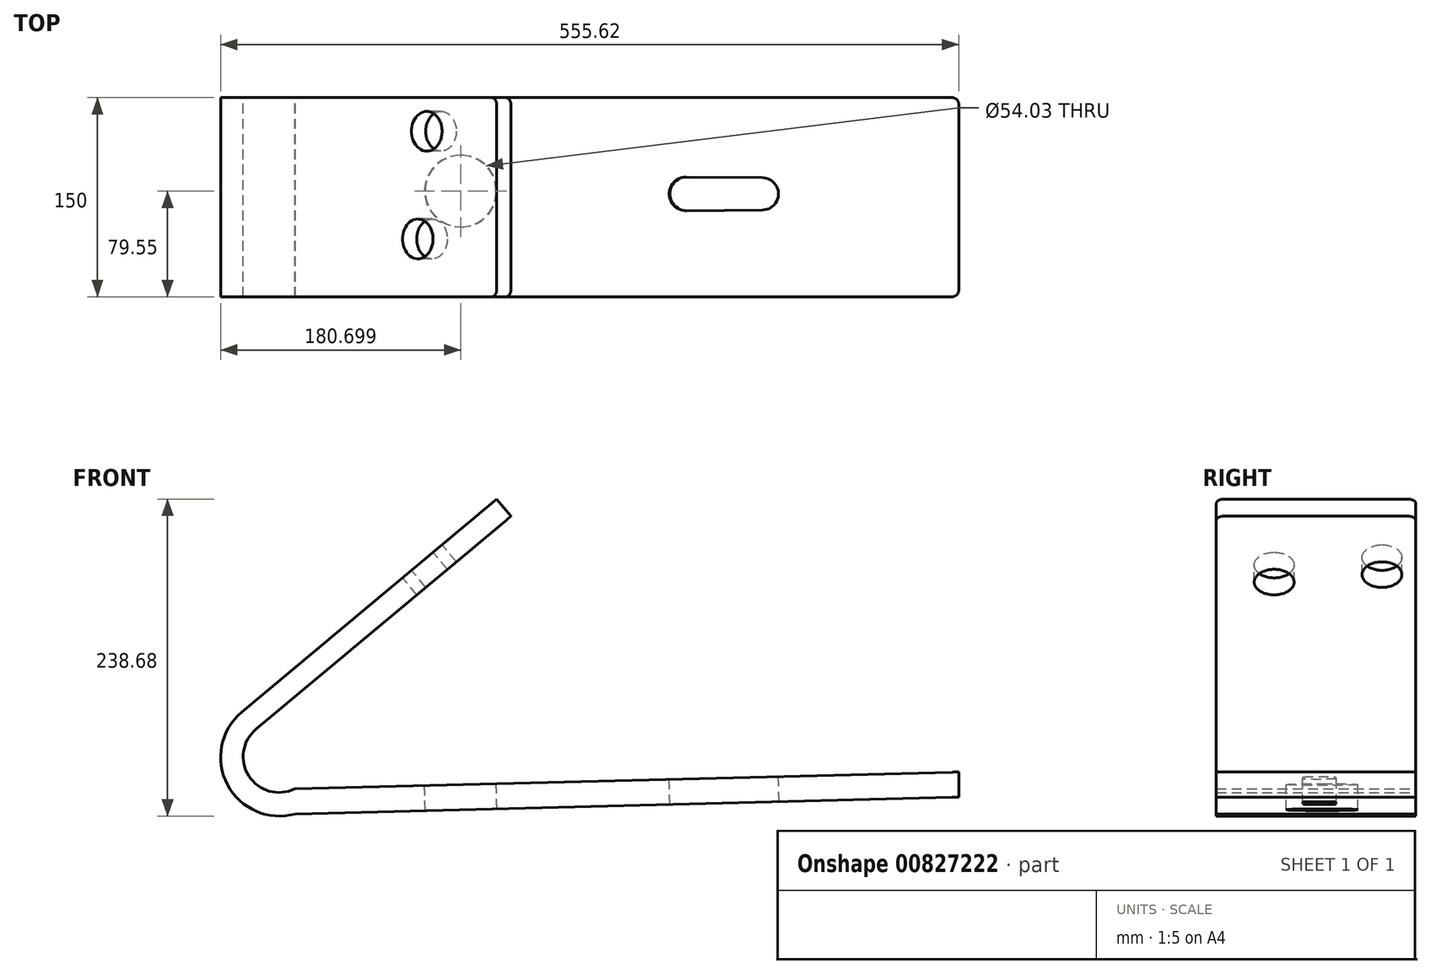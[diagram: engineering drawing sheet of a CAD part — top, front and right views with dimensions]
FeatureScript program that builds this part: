
annotation { "Feature Type Name" : "Feature", "Feature Type Description" : "" }
export const myFeature = defineFeature(function(context is Context, id is Id, definition is map)
    precondition{}
    {
        {
            var Q0;
            Q0=qCreatedBy(makeId("Front.planeOp"),FACE);
            var sketch = newSketch(context, id + "F0", { "sketchPlane" : qUnion([Q0])});
            skLineSegment(sketch, "E0", {"start": v(-98.2, -62.32) * mm, "end": v(93.63, 98) * mm});
            skLineSegment(sketch, "E1", {"start": v(93.63, 98) * mm, "end": v(104.35, 85.16) * mm});
            skLineSegment(sketch, "E2", {"start": v(104.35, 85.16) * mm, "end": v(-87.48, -75.16) * mm});
            skLineSegment(sketch, "E3", {"start": v(-98.2, -62.32) * mm, "end": v(-87.48, -75.16) * mm});
            skLineSegment(sketch, "E4", {"start": v(-58.33, -120.15) * mm, "end": v(441.5, -107.47) * mm});
            skLineSegment(sketch, "E5", {"start": v(-58.33, -120.15) * mm, "end": v(-57.85, -139.06) * mm});
            skLineSegment(sketch, "E6", {"start": v(-57.85, -139.06) * mm, "end": v(441.5, -126.4) * mm});
            skLineSegment(sketch, "E7", {"start": v(441.5, -126.4) * mm, "end": v(441.5, -107.47) * mm});
            skArc(sketch, "E8", {"start": v(-98.2, -62.32) * mm, "mid": v(-109.02, -116.99) * mm, "end": v(-57.85, -139.06) * mm});
            skArc(sketch, "E9", {"start": v(-87.48, -75.16) * mm, "mid": v(-92.82, -110.56) * mm, "end": v(-58.33, -120.15) * mm});
            skSolve(sketch);
        }
        {
            var Q0;
            Q0=makeQuery(id+"F0.imprint","IMPRINT",FACE,{"disambiguationData":[TD([[makeQuery(id+"F0.imprint","IMPRINT",EDGE,{"derivedFrom":sQuery(id+"F0.wireOp",EDGE,"E0")}),-1.0]])]});
            var Q1;
            Q1=makeQuery(id+"F0.imprint","IMPRINT",FACE,{"disambiguationData":[TD([[makeQuery(id+"F0.imprint","IMPRINT",EDGE,{"derivedFrom":sQuery(id+"F0.wireOp",EDGE,"E3")}),-1.0]])]});
            var Q2;
            Q2=makeQuery(id+"F0.imprint","IMPRINT",FACE,{"disambiguationData":[TD([[makeQuery(id+"F0.imprint","IMPRINT",EDGE,{"derivedFrom":sQuery(id+"F0.wireOp",EDGE,"E4")}),-1.0]])]});
            extrude(context, id + "F1", {"entities" : qUnion([Q0, Q1, Q2]), "depth" : 150 * mm, "offsetDistance" : 25 * mm});
        }
        {
            var Q0;
            Q0=makeQuery(id+"F1.opExtrude","CAP_EDGE",EDGE,{"disambiguationData":[OSD([sQuery(id+"F0.wireOp",EDGE,"E1")])],"isStart":false});
            var Q1;
            Q1=makeQuery(id+"F1.opExtrude","CAP_EDGE",EDGE,{"disambiguationData":[OSD([sQuery(id+"F0.wireOp",EDGE,"E1")])],"isStart":true});
            var Q2;
            Q2=makeQuery(id+"F1.opExtrude","CAP_EDGE",EDGE,{"disambiguationData":[OSD([sQuery(id+"F0.wireOp",EDGE,"E7")])],"isStart":false});
            var Q3;
            Q3=makeQuery(id+"F1.opExtrude","CAP_EDGE",EDGE,{"disambiguationData":[OSD([sQuery(id+"F0.wireOp",EDGE,"E7")])],"isStart":true});
            fillet(context, id + "F2", {"entities" : qUnion([Q0, Q1, Q2, Q3]), "radius" : 5 * mm, "tangentPropagation" : true, "allowEdgeOverflow" : false});
        }
        {
            var Q0;
            Q0=makeQuery(id+"F1.opExtrude","SWEPT_FACE",FACE,{"disambiguationData":[OSD([sQuery(id+"F0.wireOp",EDGE,"E0")])]});
            var sketch = newSketch(context, id + "F3", { "sketchPlane" : qUnion([Q0])});
            skCircle(sketch, "E10", {"center": v(66.13, -25.34) * mm, "radius": 15 * mm});
            skCircle(sketch, "E11", {"center": v(57.34, -106.48) * mm, "radius": 15 * mm});
            skSolve(sketch);
        }
        {
            var Q0;
            Q0=makeQuery(id+"F3.imprint","IMPRINT",FACE,{"disambiguationData":[TD([[makeQuery(id+"F3.imprint","IMPRINT",EDGE,{"derivedFrom":sQuery(id+"F3.wireOp",EDGE,"E11")}),1.0]])]});
            var Q1;
            Q1=makeQuery(id+"F3.imprint","IMPRINT",FACE,{"disambiguationData":[TD([[makeQuery(id+"F3.imprint","IMPRINT",EDGE,{"derivedFrom":sQuery(id+"F3.wireOp",EDGE,"E10")}),1.0]])]});
            extrude(context, id + "F4", {"entities" : qUnion([Q0, Q1]), "operationType" : NewBodyOperationType.REMOVE, "oppositeDirection" : true, "depth" : 25 * mm, "offsetDistance" : 25 * mm});
        }
        {
            var Q0;
            Q0=makeQuery(id+"F1.opExtrude","SWEPT_FACE",FACE,{"disambiguationData":[OSD([sQuery(id+"F0.wireOp",EDGE,"E4")])]});
            var sketch = newSketch(context, id + "F5", { "sketchPlane" : qUnion([Q0])});
            skCircle(sketch, "E12", {"center": v(63.36, -70.45) * mm, "radius": 27.02 * mm});
            skArc(sketch, "E13", {"start": v(233.4, -59.77) * mm, "mid": v(220.57, -72.53) * mm, "end": v(233.53, -85.18) * mm});
            skArc(sketch, "E14", {"start": v(290.85, -84.63) * mm, "mid": v(302.89, -72.47) * mm, "end": v(290.85, -60.32) * mm});
            skLineSegment(sketch, "E15", {"start": v(233.4, -59.77) * mm, "end": v(290.85, -60.32) * mm});
            skLineSegment(sketch, "E16", {"start": v(233.28, -85.18) * mm, "end": v(290.85, -84.63) * mm});
            skSolve(sketch);
        }
        {
            var Q0;
            Q0 = qSketchRegion(id + "F5", true);
            extrude(context, id + "F6", {"entities" : qUnion([Q0]), "operationType" : NewBodyOperationType.REMOVE, "oppositeDirection" : true, "depth" : 25 * mm, "offsetDistance" : 25 * mm});
        }
    });
